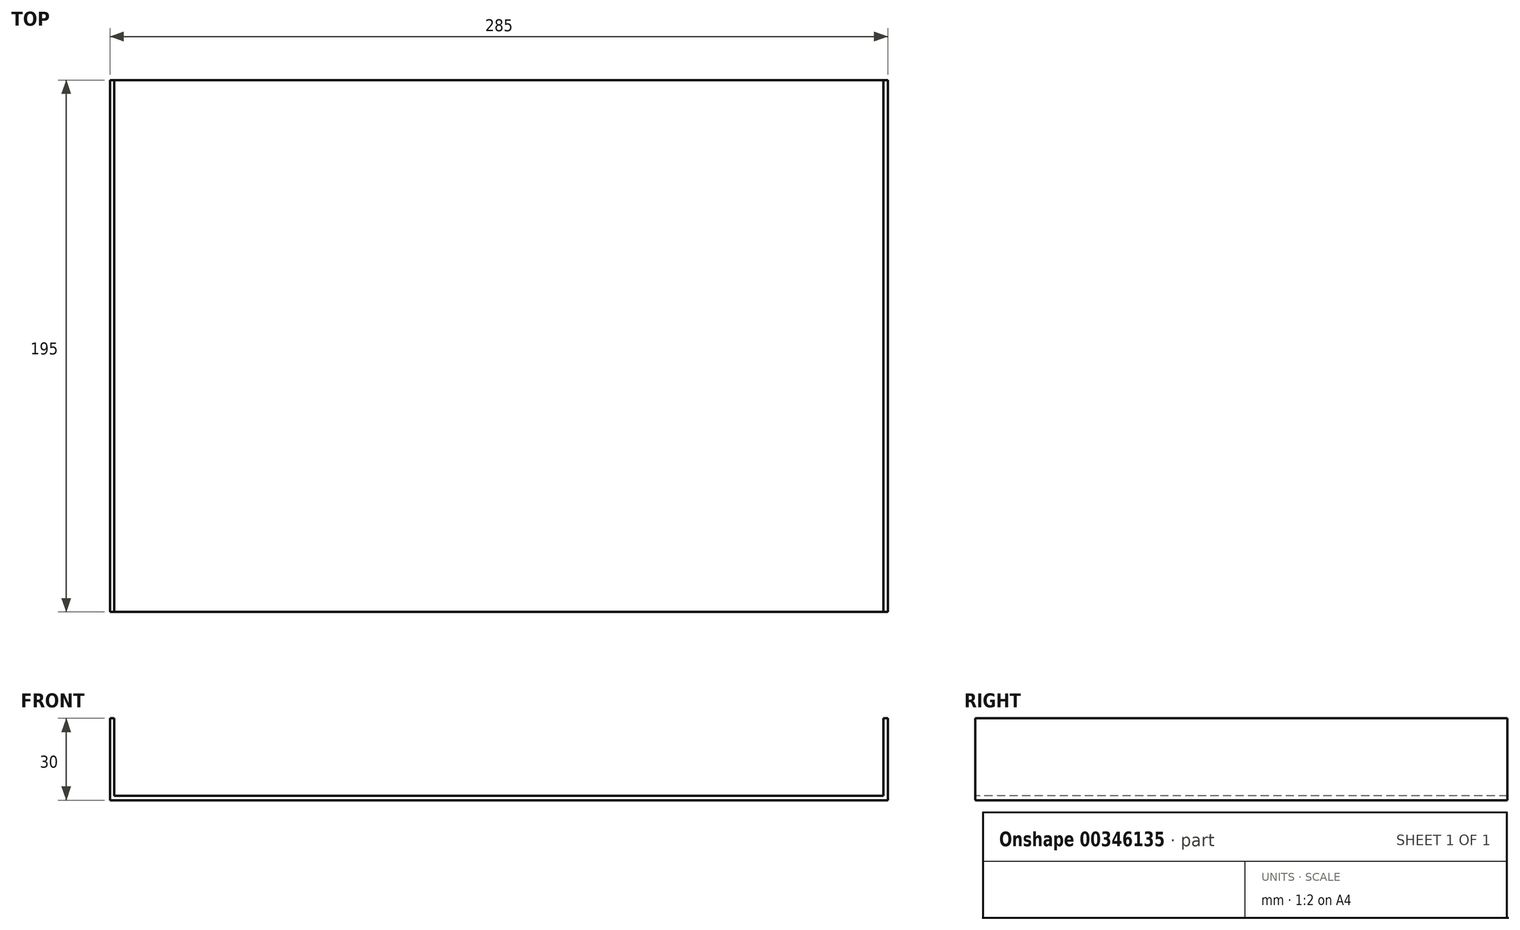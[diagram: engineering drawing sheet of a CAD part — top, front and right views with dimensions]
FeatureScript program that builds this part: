
annotation { "Feature Type Name" : "Feature", "Feature Type Description" : "" }
export const myFeature = defineFeature(function(context is Context, id is Id, definition is map)
    precondition{}
    {
        {
            var Q0;
            Q0=qCreatedBy(makeId("Top.planeOp"),FACE);
            var sketch = newSketch(context, id + "F0", { "sketchPlane" : qUnion([Q0])});
            skLineSegment(sketch, "E0.bottom", {"start": v(142.5, -97.5) * mm, "end": v(-142.5, -97.5) * mm});
            skLineSegment(sketch, "E0.top", {"start": v(142.5, 97.5) * mm, "end": v(-142.5, 97.5) * mm});
            skLineSegment(sketch, "E0.left", {"start": v(142.5, -97.5) * mm, "end": v(142.5, 97.5) * mm});
            skLineSegment(sketch, "E0.right", {"start": v(-142.5, -97.5) * mm, "end": v(-142.5, 97.5) * mm});
            skPoint(sketch, "E0.middle", {"position": v(0, 0) * mm});
            skLineSegment(sketch, "E1", {"start": v(-140.9, 97.5) * mm, "end": v(-140.9, -97.5) * mm});
            skLineSegment(sketch, "E2", {"start": v(140.9, 97.5) * mm, "end": v(140.9, -97.5) * mm});
            skSolve(sketch);
        }
        {
            var Q0;
            {var subQ0=sQuery(id+"F0.wireOp",EDGE,"E1");Q0=makeQuery(id+"F0.imprint","IMPRINT",FACE,{"disambiguationData":[TD([[makeQuery(id+"F0.imprint","IMPRINT",EDGE,{"derivedFrom":subQ0}),1.0]])]});}
            extrude(context, id + "F1", {"entities" : qUnion([Q0]), "depth" : 1.6 * mm});
        }
        {
            var Q0;
            {var subQ0=sQuery(id+"F0.wireOp",EDGE,"E0.right");Q0=makeQuery(id+"F0.imprint","IMPRINT",FACE,{"disambiguationData":[TD([[makeQuery(id+"F0.imprint","IMPRINT",EDGE,{"derivedFrom":subQ0}),-1.0]])]});}
            var Q1;
            {var subQ0=sQuery(id+"F0.wireOp",EDGE,"E0.left");Q1=makeQuery(id+"F0.imprint","IMPRINT",FACE,{"disambiguationData":[TD([[makeQuery(id+"F0.imprint","IMPRINT",EDGE,{"derivedFrom":subQ0}),1.0]])]});}
            extrude(context, id + "F2", {"entities" : qUnion([Q0, Q1]), "operationType" : NewBodyOperationType.ADD, "depth" : 30 * mm});
        }
    });
